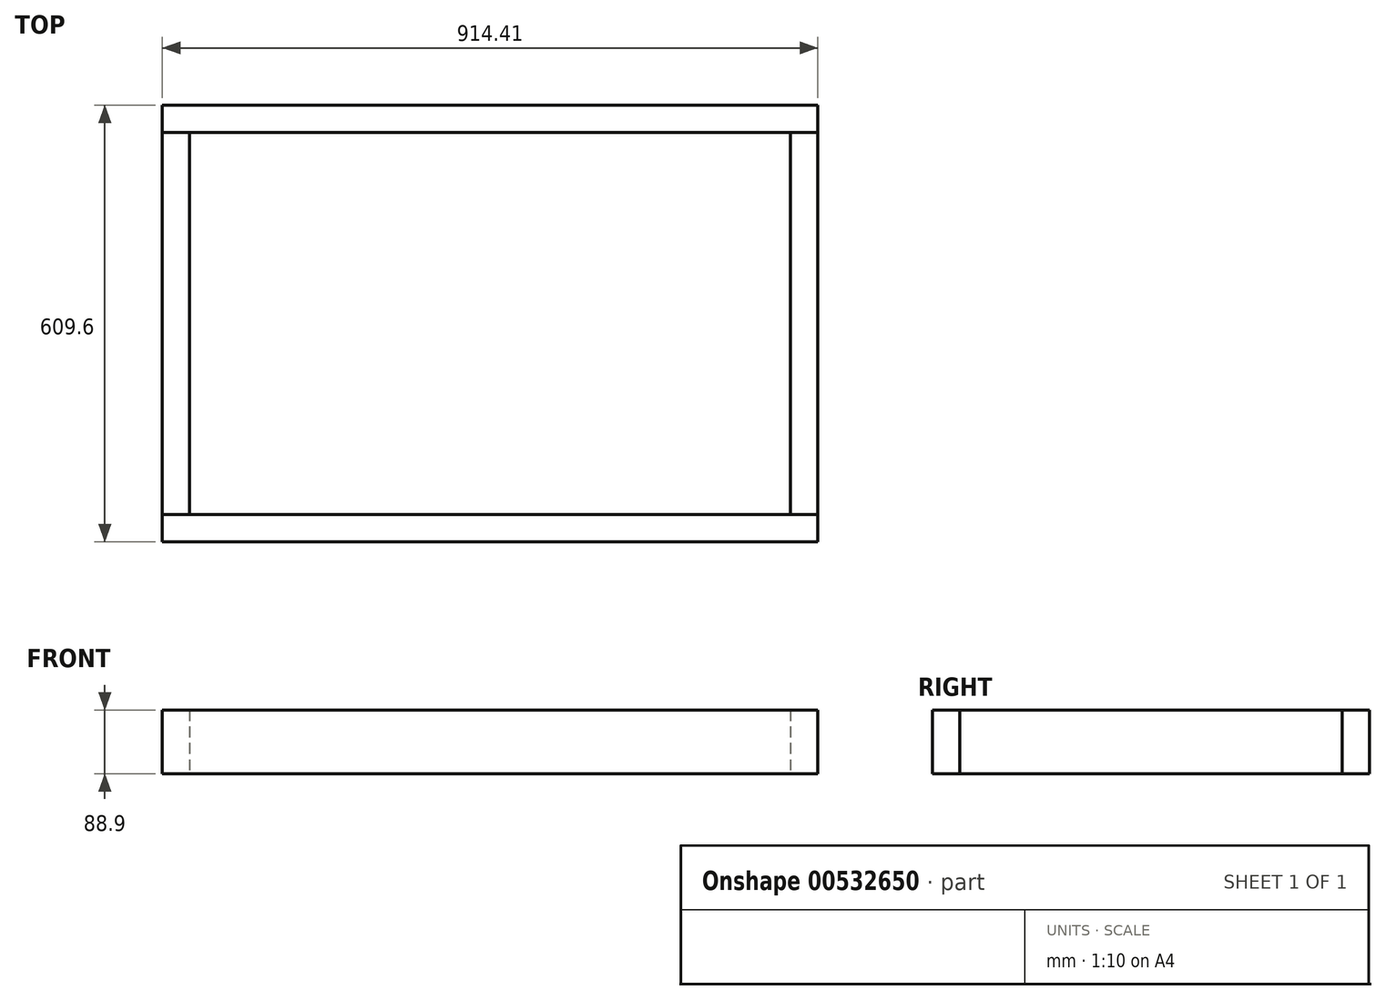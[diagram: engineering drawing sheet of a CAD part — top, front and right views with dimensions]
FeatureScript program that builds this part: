
annotation { "Feature Type Name" : "Feature", "Feature Type Description" : "" }
export const myFeature = defineFeature(function(context is Context, id is Id, definition is map)
    precondition{}
    {
        {
            var Q0;
            Q0=qCreatedBy(makeId("Top.planeOp"),FACE);
            var sketch = newSketch(context, id + "F0", { "sketchPlane" : qUnion([Q0])});
            skLineSegment(sketch, "E0.bottom", {"start": v(-328.83, -100.27) * mm, "end": v(585.57, -100.27) * mm});
            skLineSegment(sketch, "E0.top", {"start": v(-328.83, -62.17) * mm, "end": v(585.57, -62.17) * mm});
            skLineSegment(sketch, "E0.left", {"start": v(-328.83, -100.27) * mm, "end": v(-328.83, -62.17) * mm});
            skLineSegment(sketch, "E0.right", {"start": v(585.57, -100.27) * mm, "end": v(585.57, -62.17) * mm});
            skSolve(sketch);
        }
        {
            var Q0;
            Q0 = qSketchRegion(id + "F0", true);
            extrude(context, id + "F1", {"entities" : qUnion([Q0]), "depth" : 88.9 * mm, "offsetDistance" : 25.4 * mm});
        }
        {
            var Q0;
            Q0=makeQuery(id+"F1.opExtrude","SWEPT_FACE",FACE,{"disambiguationData":[OSD([sQuery(id+"F0.wireOp",EDGE,"E0.top")])]});
            var sketch = newSketch(context, id + "F2", { "sketchPlane" : qUnion([Q0])});
            skLineSegment(sketch, "E1.bottom", {"start": v(328.83, 88.9) * mm, "end": v(290.72, 88.9) * mm});
            skLineSegment(sketch, "E1.top", {"start": v(328.83, 0) * mm, "end": v(290.72, 0) * mm});
            skLineSegment(sketch, "E1.left", {"start": v(328.83, 88.9) * mm, "end": v(328.83, 0) * mm});
            skLineSegment(sketch, "E1.right", {"start": v(290.72, 88.9) * mm, "end": v(290.72, 0) * mm});
            skSolve(sketch);
        }
        {
            var Q0;
            Q0 = qSketchRegion(id + "F2", true);
            extrude(context, id + "F3", {"entities" : qUnion([Q0]), "depth" : 533.4 * mm, "offsetDistance" : 25.4 * mm});
        }
        {
            var Q0;
            Q0=makeQuery(id+"F3.opExtrude","SWEPT_BODY",BODY,{"disambiguationData":[OSD([sQuery(id+"F2.wireOp",EDGE,"E1.bottom"),sQuery(id+"F2.wireOp",EDGE,"E1.top"),sQuery(id+"F2.wireOp",EDGE,"E1.left"),sQuery(id+"F2.wireOp",EDGE,"E1.right")])]});
            transform(context, id + "F4", {"entities" : qUnion([Q0]), "transformType" : TransformType.TRANSLATION_3D, "dx" : 876.3 * mm, "dy" : 0 * mm, "dz" : 0 * mm, "makeCopy" : true});
        }
        {
            var Q0;
            Q0=makeQuery(id+"F1.opExtrude","SWEPT_BODY",BODY,{"disambiguationData":[OSD([sQuery(id+"F0.wireOp",EDGE,"E0.bottom"),sQuery(id+"F0.wireOp",EDGE,"E0.top"),sQuery(id+"F0.wireOp",EDGE,"E0.left"),sQuery(id+"F0.wireOp",EDGE,"E0.right")])]});
            transform(context, id + "F5", {"entities" : qUnion([Q0]), "transformType" : TransformType.TRANSLATION_3D, "dx" : 0 * mm, "dy" : 571.5 * mm, "dz" : 0 * mm, "makeCopy" : true});
        }
    });
